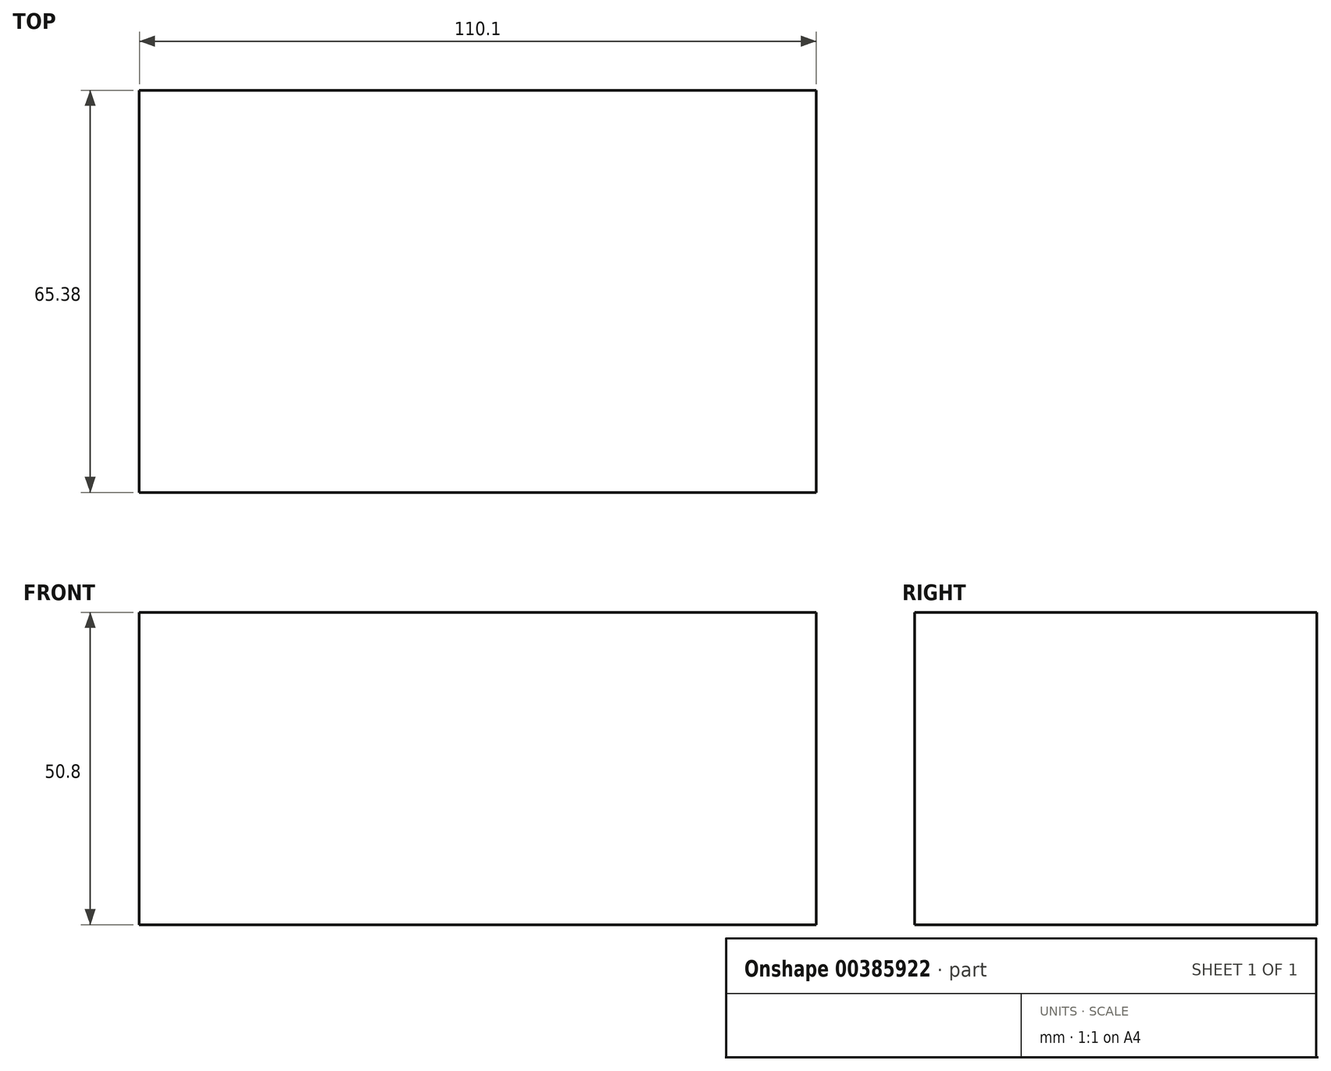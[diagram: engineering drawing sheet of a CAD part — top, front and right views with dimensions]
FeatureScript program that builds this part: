
annotation { "Feature Type Name" : "Feature", "Feature Type Description" : "" }
export const myFeature = defineFeature(function(context is Context, id is Id, definition is map)
    precondition{}
    {
        {
            var Q0;
            Q0=qCreatedBy(makeId("Top.planeOp"),FACE);
            var sketch = newSketch(context, id + "F0", { "sketchPlane" : qUnion([Q0])});
            skLineSegment(sketch, "E0", {"start": v(-58.44, 65.38) * mm, "end": v(-58.44, 0) * mm});
            skLineSegment(sketch, "E1", {"start": v(-58.44, 0) * mm, "end": v(51.66, 0) * mm});
            skLineSegment(sketch, "E2", {"start": v(51.66, 0) * mm, "end": v(51.66, 65.38) * mm});
            skLineSegment(sketch, "E3", {"start": v(51.66, 65.38) * mm, "end": v(-58.44, 65.38) * mm});
            skSolve(sketch);
        }
        {
            var Q0;
            Q0=makeQuery(id+"F0.imprint","IMPRINT",FACE,{"disambiguationData":[TD([[makeQuery(id+"F0.imprint","IMPRINT",EDGE,{"derivedFrom":sQuery(id+"F0.wireOp",EDGE,"E0")}),1.0]])]});
            extrude(context, id + "F1", {"entities" : qUnion([Q0]), "depth" : 50.8 * mm});
        }
    });
